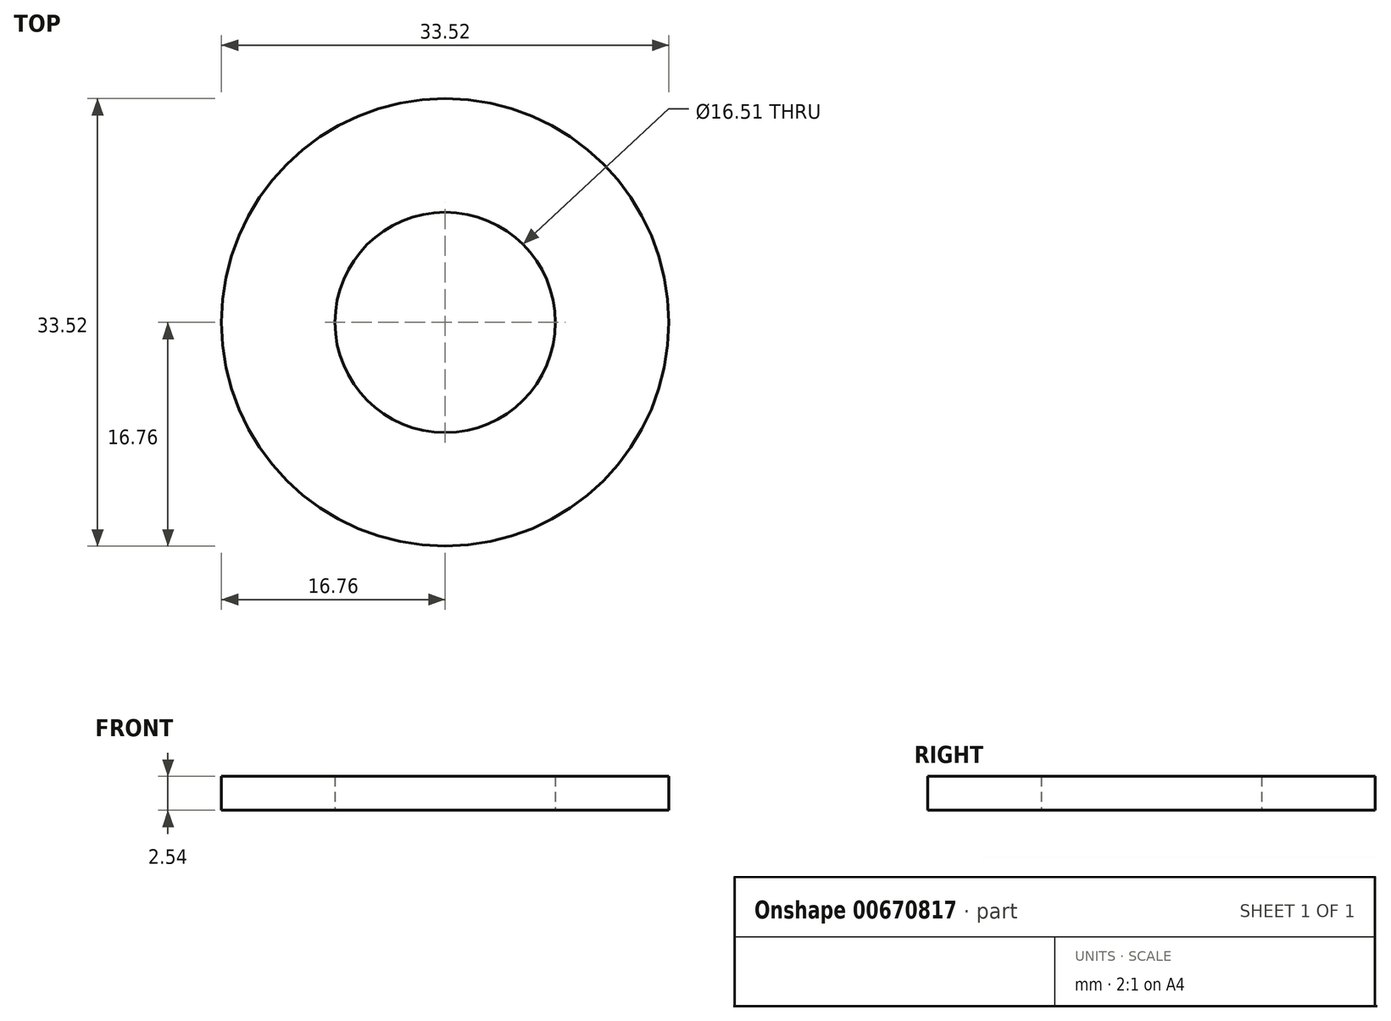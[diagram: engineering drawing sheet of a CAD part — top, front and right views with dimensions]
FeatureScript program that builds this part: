
annotation { "Feature Type Name" : "Feature", "Feature Type Description" : "" }
export const myFeature = defineFeature(function(context is Context, id is Id, definition is map)
    precondition{}
    {
        {
            var Q0;
            Q0=qCreatedBy(makeId("Top.planeOp"),FACE);
            var sketch = newSketch(context, id + "F0", { "sketchPlane" : qUnion([Q0])});
            skCircle(sketch, "E0", {"center": v(0, 0) * mm, "radius": 16.76 * mm});
            skCircle(sketch, "E1", {"center": v(0, 0) * mm, "radius": 8.26 * mm});
            skSolve(sketch);
        }
        {
            var Q0;
            Q0 = qSketchRegion(id + "F0", true);
            extrude(context, id + "F1", {"entities" : qUnion([Q0]), "domain" : OperationDomain.MODEL, "flatOperationType" : FlatOperationType.REMOVE, "depth" : 2.54 * mm, "offsetDistance" : 25.4 * mm});
        }
    });
